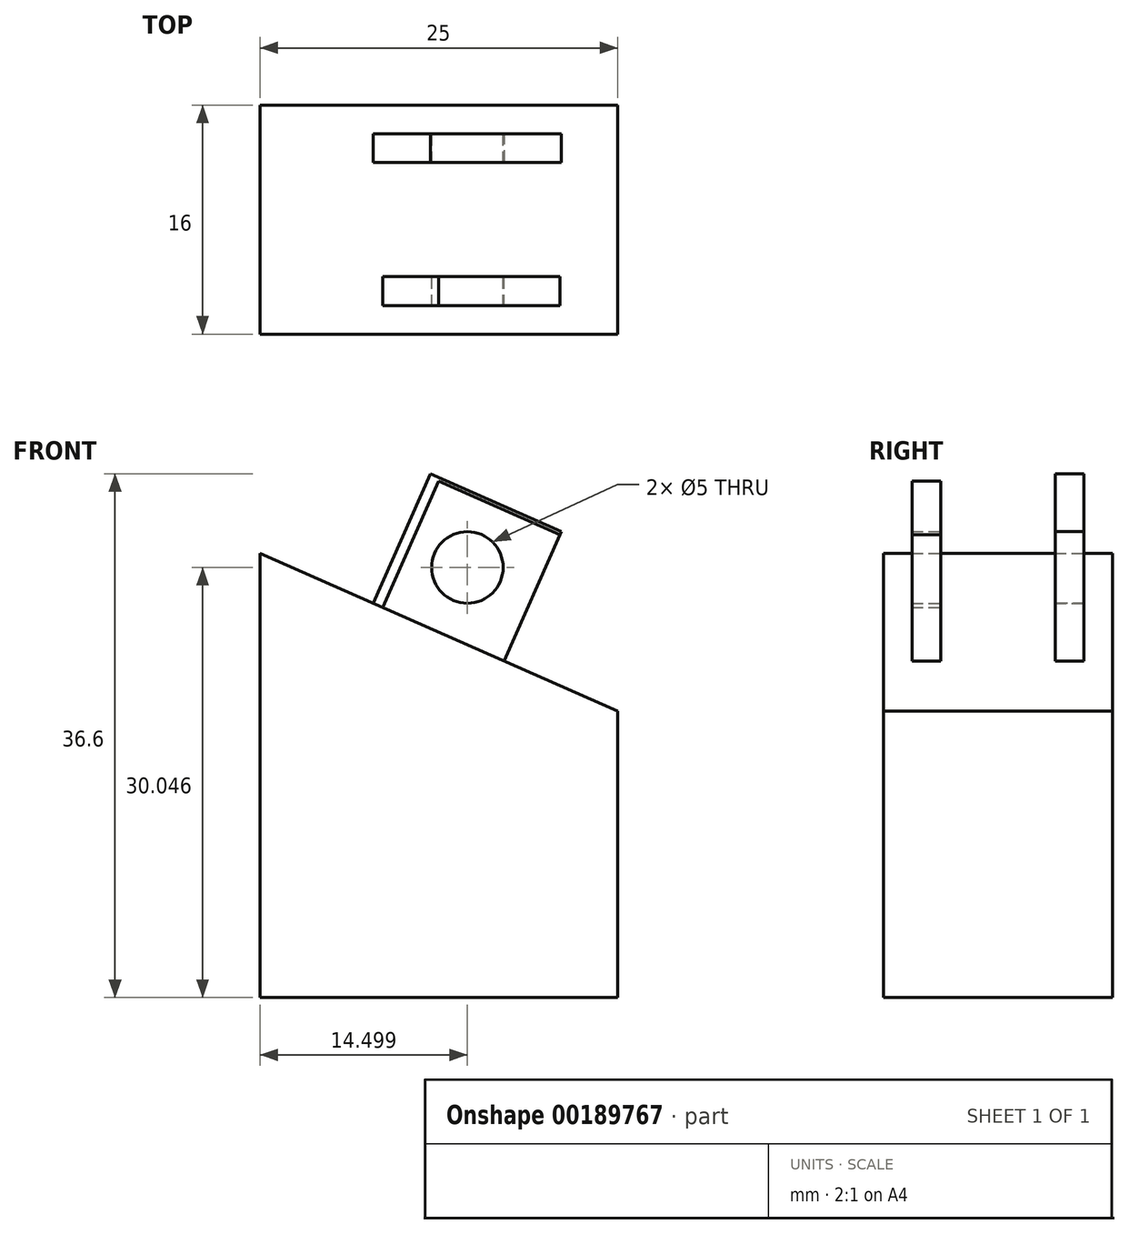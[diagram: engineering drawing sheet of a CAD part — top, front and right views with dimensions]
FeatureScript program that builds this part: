
annotation { "Feature Type Name" : "Feature", "Feature Type Description" : "" }
export const myFeature = defineFeature(function(context is Context, id is Id, definition is map)
    precondition{}
    {
        {
            var Q0;
            Q0=qCreatedBy(makeId("Front.planeOp"),FACE);
            var sketch = newSketch(context, id + "F0", { "sketchPlane" : qUnion([Q0])});
            skLineSegment(sketch, "E0", {"start": v(0, 0) * mm, "end": v(-25, 0) * mm});
            skLineSegment(sketch, "E1", {"start": v(-25, 0) * mm, "end": v(-25, 31.03) * mm});
            skLineSegment(sketch, "E2", {"start": v(-25, 31.03) * mm, "end": v(0, 20) * mm});
            skLineSegment(sketch, "E3", {"start": v(0, 20) * mm, "end": v(0, 0) * mm});
            skSolve(sketch);
        }
        {
            var Q0;
            Q0=makeQuery(id+"F0.imprint","IMPRINT",FACE,{"disambiguationData":[TD([[makeQuery(id+"F0.imprint","IMPRINT",EDGE,{"derivedFrom":sQuery(id+"F0.wireOp",EDGE,"E0")}),-1.0]])]});
            extrude(context, id + "F1", {"entities" : qUnion([Q0]), "depth" : 16 * mm});
        }
        {
            var Q0;
            Q0=makeQuery(id+"F1.opExtrude","SWEPT_FACE",FACE,{"disambiguationData":[OSD([sQuery(id+"F0.wireOp",EDGE,"E2")])]});
            var sketch = newSketch(context, id + "F2", { "sketchPlane" : qUnion([Q0])});
            skLineSegment(sketch, "E4", {"start": v(-21.74, -16) * mm, "end": v(-21.74, -14) * mm, "construction": true});
            skLineSegment(sketch, "E5", {"start": v(-21.74, 0) * mm, "end": v(-21.74, -2) * mm, "construction": true});
            skLineSegment(sketch, "E6", {"start": v(-21.74, -2) * mm, "end": v(-16.74, -2) * mm, "construction": true});
            skLineSegment(sketch, "E7.bottom", {"start": v(-16.74, -2) * mm, "end": v(-26.74, -2) * mm});
            skLineSegment(sketch, "E7.top", {"start": v(-16.74, -4) * mm, "end": v(-26.74, -4) * mm});
            skLineSegment(sketch, "E7.left", {"start": v(-16.74, -2) * mm, "end": v(-16.74, -4) * mm});
            skLineSegment(sketch, "E7.right", {"start": v(-26.74, -2) * mm, "end": v(-26.74, -4) * mm});
            skLineSegment(sketch, "E8", {"start": v(-21.74, -14) * mm, "end": v(-16.73, -14) * mm, "construction": true});
            skLineSegment(sketch, "E9.bottom", {"start": v(-16.73, -14) * mm, "end": v(-26, -14) * mm});
            skLineSegment(sketch, "E9.top", {"start": v(-16.73, -12) * mm, "end": v(-26, -12) * mm});
            skLineSegment(sketch, "E9.left", {"start": v(-16.73, -14) * mm, "end": v(-16.73, -12) * mm});
            skLineSegment(sketch, "E9.right", {"start": v(-26, -14) * mm, "end": v(-26, -12) * mm});
            skSolve(sketch);
        }
        {
            var Q0;
            Q0=makeQuery(id+"F2.imprint","IMPRINT",FACE,{"disambiguationData":[TD([[makeQuery(id+"F2.imprint","IMPRINT",EDGE,{"derivedFrom":sQuery(id+"F2.wireOp",EDGE,"E7.bottom")}),1.0]])]});
            extrude(context, id + "F3", {"entities" : qUnion([Q0]), "operationType" : NewBodyOperationType.ADD, "depth" : 9.9 * mm});
        }
        {
            var Q0;
            Q0 = qSketchRegion(id + "F2", true);
            extrude(context, id + "F4", {"entities" : qUnion([Q0]), "operationType" : NewBodyOperationType.ADD, "depth" : 9.65 * mm});
        }
        {
            var Q0;
            Q0=makeQuery(id+"F3.opExtrude","SWEPT_FACE",FACE,{"disambiguationData":[OSD([sQuery(id+"F2.wireOp",EDGE,"E7.bottom")])]});
            var sketch = newSketch(context, id + "F5", { "sketchPlane" : qUnion([Q0])});
            skLineSegment(sketch, "E10", {"start": v(8.5, 34.58) * mm, "end": v(12.5, 25.51) * mm, "construction": true});
            skLineSegment(sketch, "E11", {"start": v(5.93, 28.03) * mm, "end": v(15.08, 32.06) * mm, "construction": true});
            skCircle(sketch, "E12", {"center": v(10.5, 30.05) * mm, "radius": 2.5 * mm});
            skSolve(sketch);
        }
        {
            var Q0;
            Q0=makeQuery(id+"F5.imprint","IMPRINT",FACE,{"disambiguationData":[TD([[makeQuery(id+"F5.imprint","IMPRINT",EDGE,{"derivedFrom":sQuery(id+"F5.wireOp",EDGE,"E12")}),1.0]])]});
            var Q1;
            Q1=sQuery(id+"F5.wireOp",EDGE,"E12");
            extrude(context, id + "F6", {"entities" : qUnion([Q0]), "operationType" : NewBodyOperationType.REMOVE, "surfaceEntities" : qUnion([Q1]), "oppositeDirection" : true, "depth" : 17.5 * mm});
        }
    });
